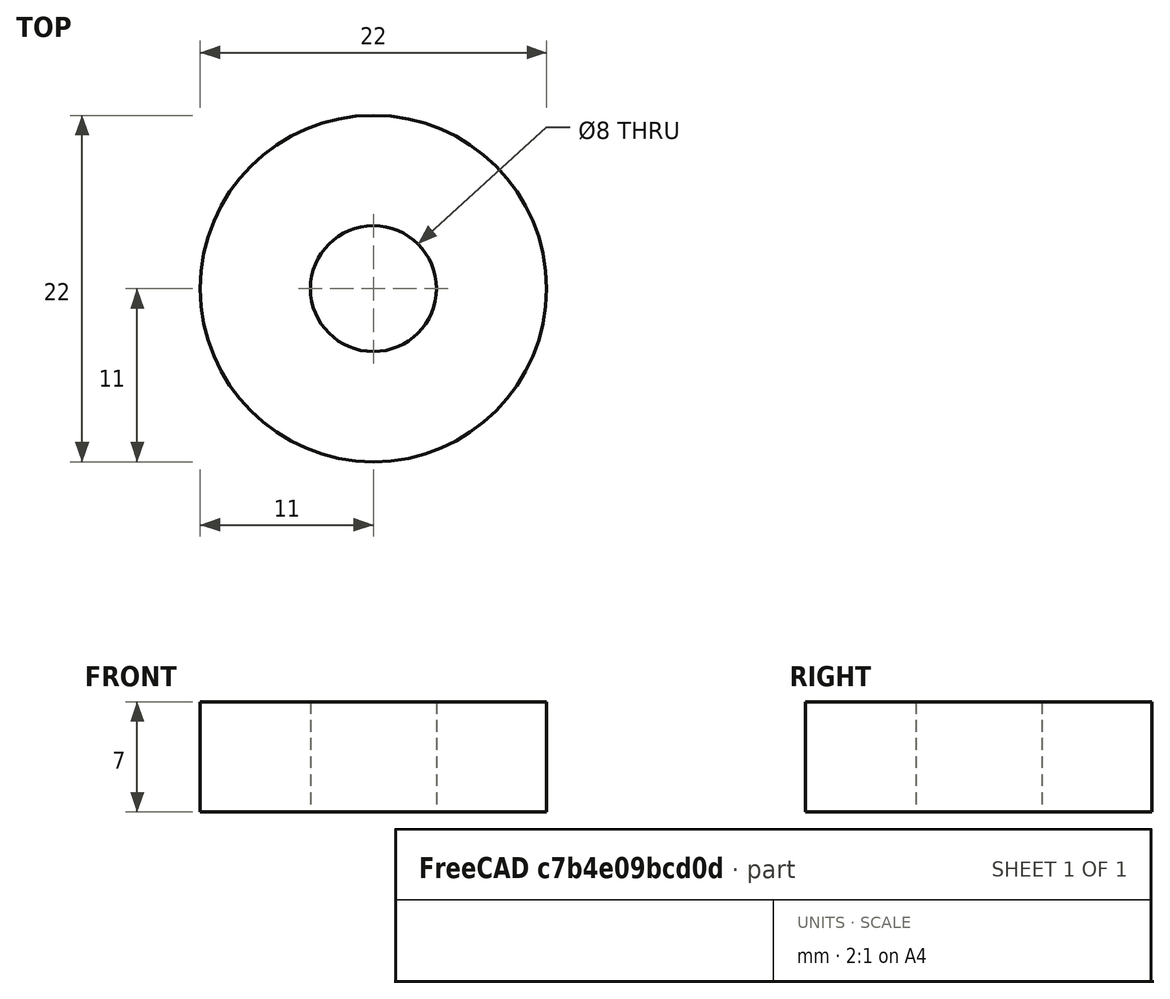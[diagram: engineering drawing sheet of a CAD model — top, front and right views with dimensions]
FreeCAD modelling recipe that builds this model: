
FCSTD DOCUMENT  (FreeCAD 0.14R3700 (Git))
Label: BR_Roulement
License: CC-BY 3.0
LicenseURL: http://creativecommons.org/licenses/by/3.0/
objects: Sketcher::SketchObject×1, Part::Revolution×1, Part::Feature×1
note: 3 computed .brp shape members not serialized (recipe doc carries the construction recipe); baked Part::Feature solids carry a one-line shape summary decoded from their .brp

FEATURE [Sketcher::SketchObject] Sketch
  Placement = pos=(0,0,0) rot=(-1,0,0;4.71239rad)
  sketch-geometry (4):
    g0: LineSegment StartX=-11 StartY=7 StartZ=0 EndX=-4 EndY=7 EndZ=0
    g1: LineSegment StartX=-4 StartY=7 StartZ=0 EndX=-4 EndY=0 EndZ=0
    g2: LineSegment StartX=-4 StartY=0 StartZ=0 EndX=-11 EndY=0 EndZ=0
    g3: LineSegment StartX=-11 StartY=0 StartZ=0 EndX=-11 EndY=7 EndZ=0
  constraints (12):
    c: Coincident(g0,g1)
    c: Coincident(g1,g2)
    c: Coincident(g2,g3)
    c: Coincident(g3,g0)
    c: Horizontal(g0)
    c: Horizontal(g2)
    c: Vertical(g1)
    c: Vertical(g3)
    c: PointOnObject(g1,g-1)
    c: DistanceX(g-1,g1) = -4
    c: DistanceX(g-1,g2) = -11
    c: DistanceY(g3) = 7
FEATURE [Part::Revolution] Revolve
  Angle = 360
  Axis = (0,0,1)
  Base = (0,0,0)
  Solid = false
  Source = -> Sketch
FEATURE [Part::Feature] Revolve001  label="Roulement"
  shape: bbox 22 x 22 x 7 mm, 4 faces, 0 solids (baked)
